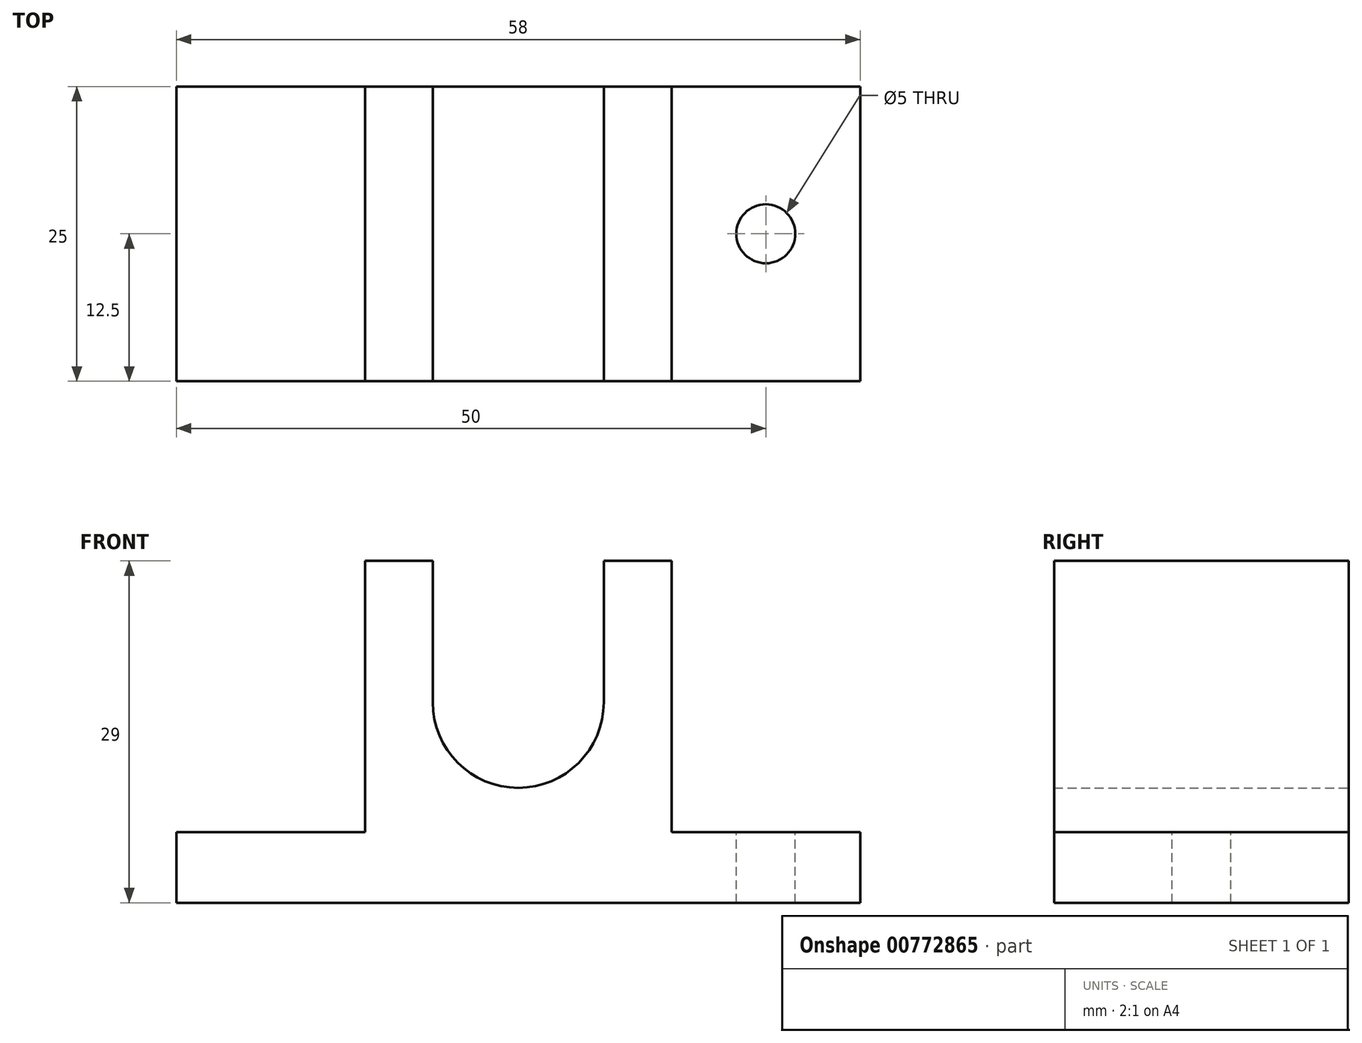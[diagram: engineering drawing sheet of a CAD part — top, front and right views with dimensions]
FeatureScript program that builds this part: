
annotation { "Feature Type Name" : "Feature", "Feature Type Description" : "" }
export const myFeature = defineFeature(function(context is Context, id is Id, definition is map)
    precondition{}
    {
        {
            var Q0;
            Q0=qCreatedBy(makeId("Front.planeOp"),FACE);
            var sketch = newSketch(context, id + "F0", { "sketchPlane" : qUnion([Q0])});
            skArc(sketch, "E0", {"start": v(-13, 0) * mm, "mid": v(0, -13) * mm, "end": v(13, 0) * mm});
            skArc(sketch, "E1", {"start": v(-7.25, 0) * mm, "mid": v(0, -7.25) * mm, "end": v(7.25, 0) * mm});
            skLineSegment(sketch, "E2", {"start": v(-13, 0) * mm, "end": v(-13, -11) * mm});
            skLineSegment(sketch, "E3", {"start": v(-13, -11) * mm, "end": v(-29, -11) * mm});
            skLineSegment(sketch, "E4", {"start": v(-29, -11) * mm, "end": v(-29, -17) * mm});
            skLineSegment(sketch, "E5.MirrorCS", {"start": v(13, 0) * mm, "end": v(13, -11) * mm});
            skLineSegment(sketch, "E6.MirrorCS", {"start": v(13, -11) * mm, "end": v(29, -11) * mm});
            skLineSegment(sketch, "E7.MirrorCS", {"start": v(29, -11) * mm, "end": v(29, -17) * mm});
            skLineSegment(sketch, "E8", {"start": v(-29, -17) * mm, "end": v(29, -17) * mm});
            skLineSegment(sketch, "E9.top", {"start": v(-13, 12) * mm, "end": v(-7.25, 12) * mm});
            skLineSegment(sketch, "E9.left", {"start": v(-13, 0) * mm, "end": v(-13, 12) * mm});
            skLineSegment(sketch, "E9.right", {"start": v(-7.25, 0) * mm, "end": v(-7.25, 12) * mm});
            skLineSegment(sketch, "E10.MirrorCS", {"start": v(7.25, 0) * mm, "end": v(7.25, 12) * mm});
            skLineSegment(sketch, "E11.MirrorCS", {"start": v(13, 0) * mm, "end": v(13, 12) * mm});
            skLineSegment(sketch, "E12.MirrorCS", {"start": v(13, 12) * mm, "end": v(7.25, 12) * mm});
            skSolve(sketch);
        }
        {
            var Q0;
            {var subQ4=sQuery(id+"F0.wireOp",EDGE,"5oKvWmHt-1vnq-7eWD-vFe3-7jsL7B6FlRV2");Q0=makeQuery(id+"F0.imprint","IMPRINT",FACE,{"disambiguationData":[TD([[makeQuery(id+"F0.imprint","IMPRINT",EDGE,{"derivedFrom":subQ4}),1.0]])]});}
            var Q1;
            {var subQ0=sQuery(id+"F0.wireOp",EDGE,"E2");Q1=makeQuery(id+"F0.imprint","IMPRINT",FACE,{"disambiguationData":[TD([[makeQuery(id+"F0.imprint","IMPRINT",EDGE,{"derivedFrom":subQ0}),1.0]])]});}
            var Q2;
            Q2=makeQuery(id+"F0.imprint","IMPRINT",FACE,{"disambiguationData":[TD([[makeQuery(id+"F0.imprint","IMPRINT",EDGE,{"derivedFrom":sQuery(id+"F0.wireOp",EDGE,"E0")}),1.0]])]});
            extrude(context, id + "F1", {"entities" : qUnion([Q0, Q1, Q2]), "depth" : 25 * mm, "offsetDistance" : 25 * mm});
        }
        {
            var Q0;
            Q0=makeQuery(id+"F1.opExtrude","SWEPT_FACE",FACE,{"disambiguationData":[OSD([sQuery(id+"F0.wireOp",EDGE,"E6.MirrorCS")])]});
            var sketch = newSketch(context, id + "F2", { "sketchPlane" : qUnion([Q0])});
            skCircle(sketch, "E13", {"center": v(21, -12.5) * mm, "radius": 2.5 * mm});
            skPoint(sketch, "E14.orphan", {"position": v(21, 0) * mm});
            skCircle(sketch, "E15.MirrorC", {"center": v(-21, -12.5) * mm, "radius": 2.5 * mm});
            skSolve(sketch);
        }
        {
            var Q0;
            Q0=makeQuery(id+"F2.imprint","IMPRINT",FACE,{"disambiguationData":[TD([[makeQuery(id+"F2.imprint","IMPRINT",EDGE,{"derivedFrom":sQuery(id+"F2.wireOp",EDGE,"E13")}),1.0]])]});
            var Q1;
            Q1=makeQuery(id+"F2.imprint","IMPRINT",FACE,{"disambiguationData":[TD([[makeQuery(id+"F2.imprint","IMPRINT",EDGE,{"derivedFrom":sQuery(id+"F2.wireOp",EDGE,"E15.MirrorC")}),-1.0]])]});
            extrude(context, id + "F3", {"entities" : qUnion([Q0, Q1]), "operationType" : NewBodyOperationType.REMOVE, "endBound" : BoundingType.THROUGH_ALL, "oppositeDirection" : true, "depth" : 25 * mm, "offsetDistance" : 25 * mm});
        }
    });
